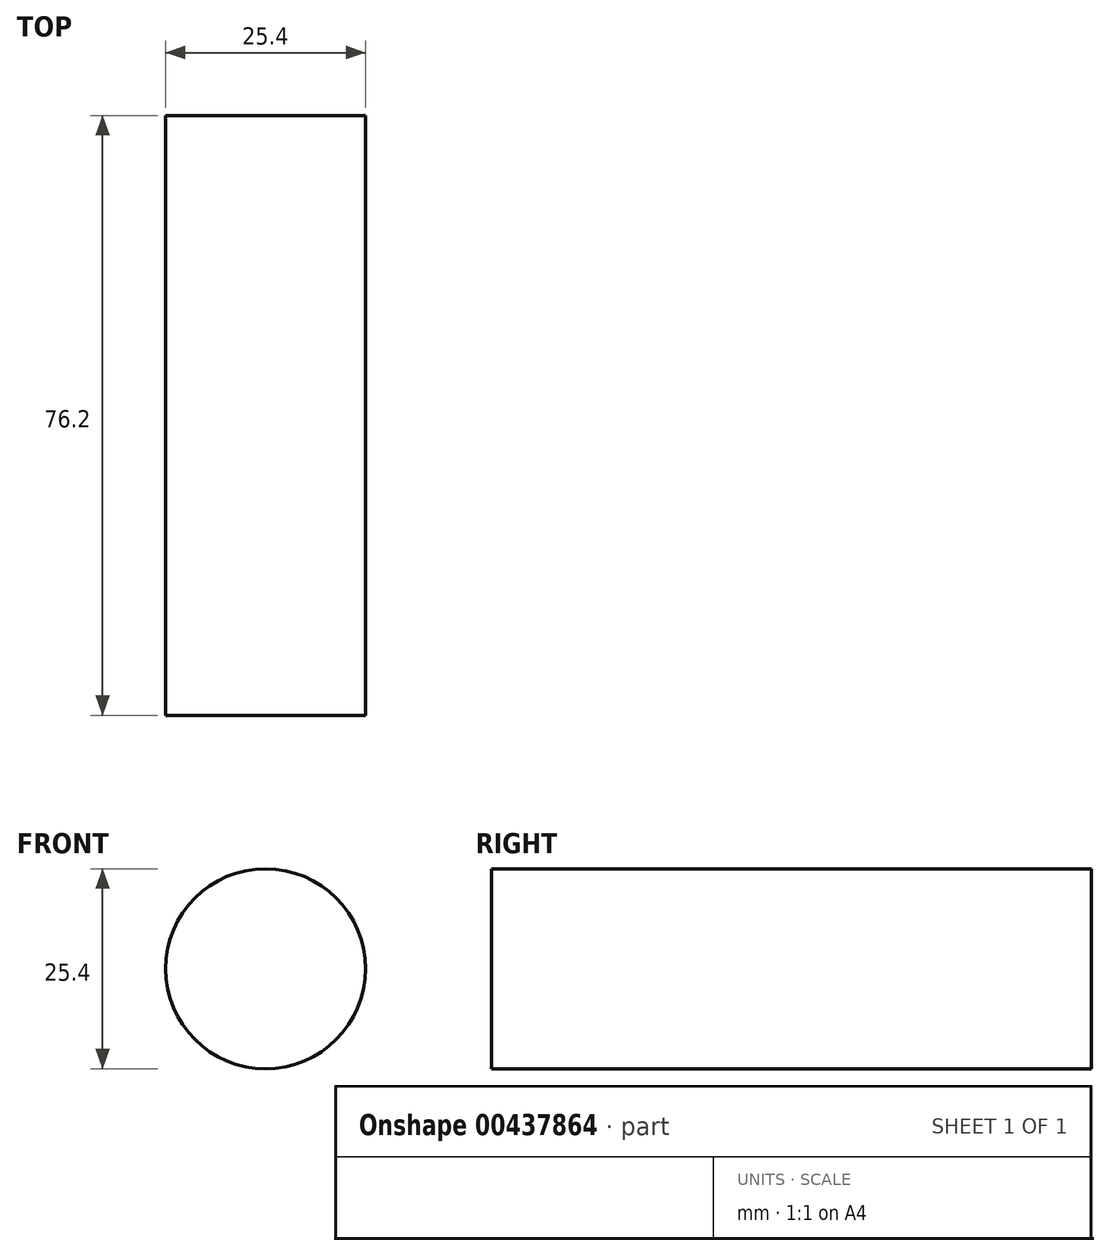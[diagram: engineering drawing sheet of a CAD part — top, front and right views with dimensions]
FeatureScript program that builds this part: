
annotation { "Feature Type Name" : "Feature", "Feature Type Description" : "" }
export const myFeature = defineFeature(function(context is Context, id is Id, definition is map)
    precondition{}
    {
        {
            var Q0;
            Q0=qCreatedBy(makeId("Front.planeOp"),FACE);
            var sketch = newSketch(context, id + "F0", { "sketchPlane" : qUnion([Q0])});
            skCircle(sketch, "E0", {"center": v(-5.76, 24.57) * mm, "radius": 12.7 * mm});
            skSolve(sketch);
        }
        {
            var Q0;
            Q0 = qSketchRegion(id + "F0", true);
            extrude(context, id + "F1", {"entities" : qUnion([Q0]), "depth" : 76.2 * mm});
        }
    });
